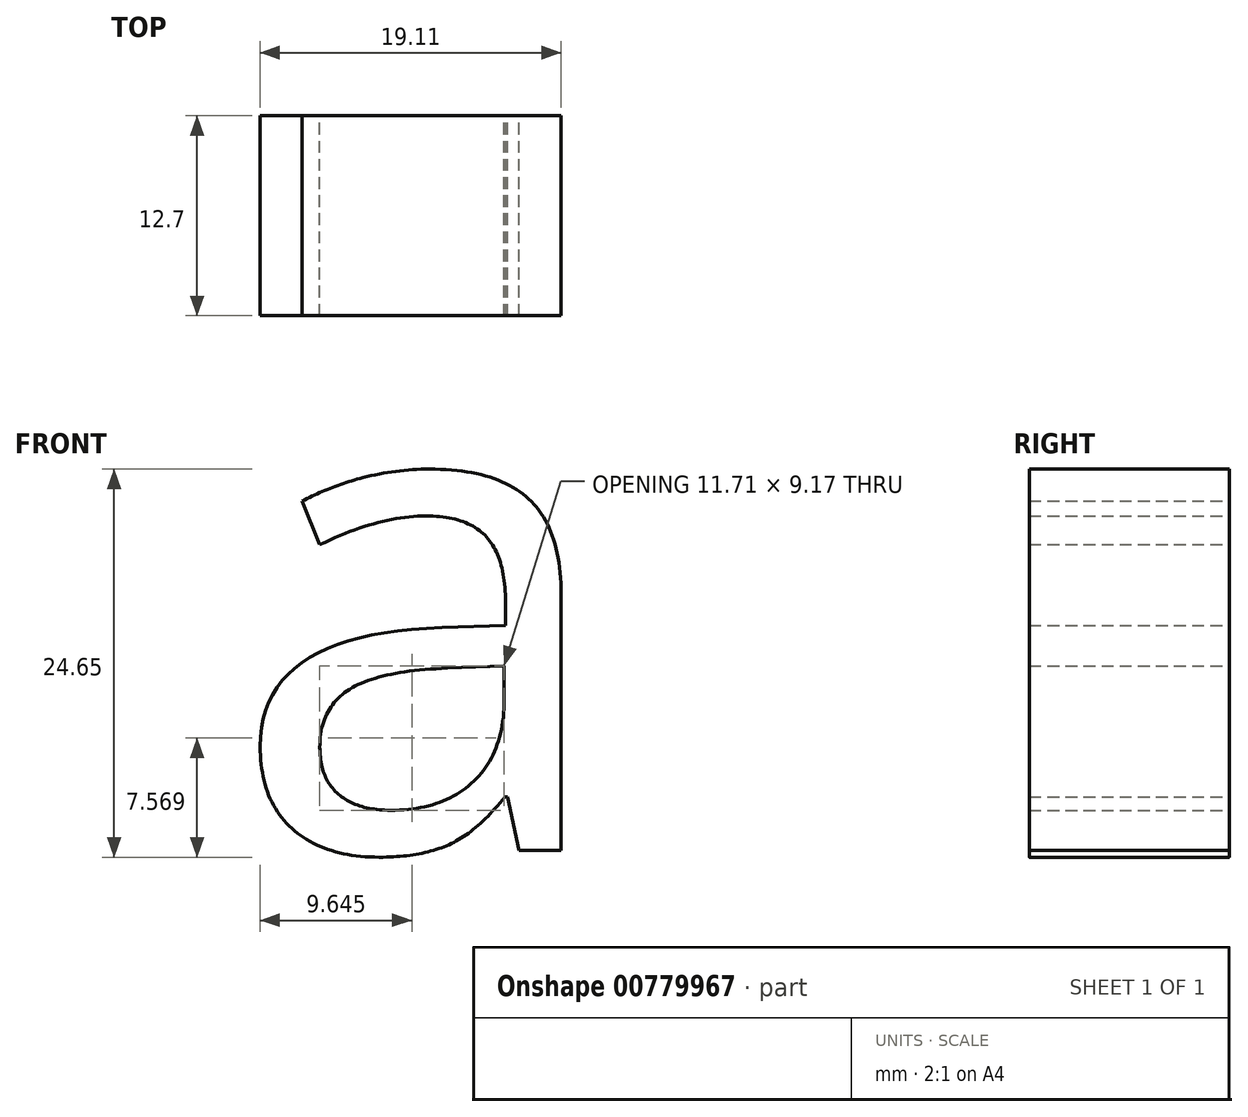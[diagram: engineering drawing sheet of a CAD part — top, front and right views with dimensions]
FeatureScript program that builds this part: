
annotation { "Feature Type Name" : "Feature", "Feature Type Description" : "" }
export const myFeature = defineFeature(function(context is Context, id is Id, definition is map)
    precondition{}
    {
        {
            var Q0;
            Q0=qCreatedBy(makeId("Front.planeOp"),FACE);
            var sketch = newSketch(context, id + "F0", { "sketchPlane" : qUnion([Q0])});
            skText(sketch, "E0", { "text": "a", "fontName": "OpenSans-Regular.ttf"});
            const initialGuessF0  = {"E0": [-0.05854, 0, 1, 0, 0.03205]};
            skSetInitialGuess(sketch, initialGuessF0);
            skSolve(sketch);
        }
        {
            var Q0;
            Q0 = qSketchRegion(id + "F0", true);
            extrude(context, id + "F1", {"entities" : qUnion([Q0]), "depth" : 12.7 * mm, "offsetDistance" : 25.4 * mm});
        }
    });
